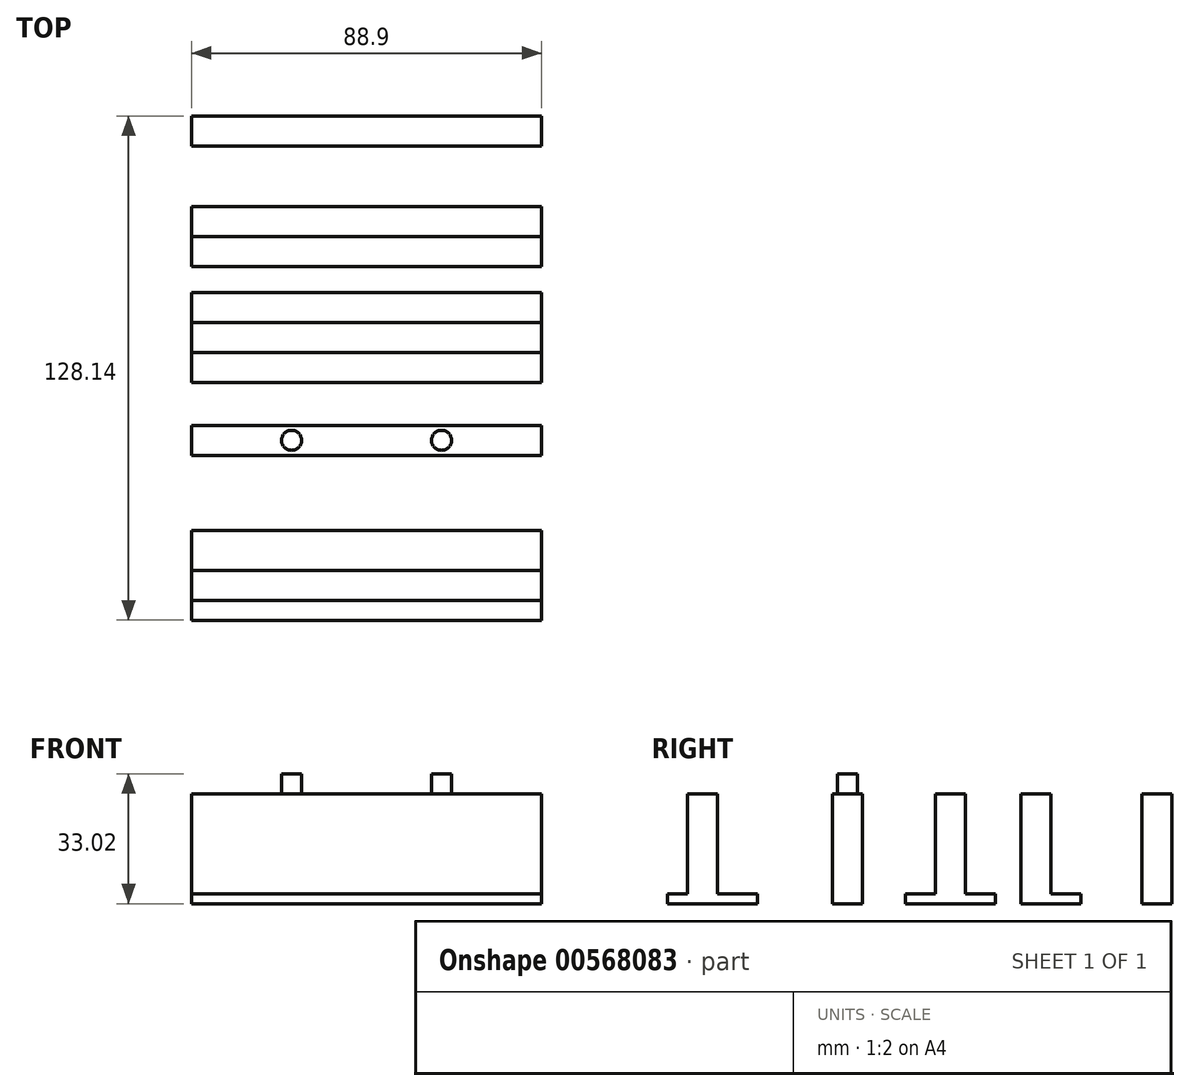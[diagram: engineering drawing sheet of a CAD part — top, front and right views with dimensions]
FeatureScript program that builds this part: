
annotation { "Feature Type Name" : "Feature", "Feature Type Description" : "" }
export const myFeature = defineFeature(function(context is Context, id is Id, definition is map)
    precondition{}
    {
        {
            var Q0;
            Q0=qCreatedBy(makeId("Top.planeOp"),FACE);
            var sketch = newSketch(context, id + "F0", { "sketchPlane" : qUnion([Q0])});
            skLineSegment(sketch, "E0.bottom", {"start": v(-25.4, 22.86) * mm, "end": v(63.5, 22.86) * mm});
            skLineSegment(sketch, "E0.top", {"start": v(-25.4, 15.24) * mm, "end": v(63.5, 15.24) * mm});
            skLineSegment(sketch, "E0.left", {"start": v(-25.4, 22.86) * mm, "end": v(-25.4, 15.24) * mm});
            skLineSegment(sketch, "E0.right", {"start": v(63.5, 22.86) * mm, "end": v(63.5, 15.24) * mm});
            skLineSegment(sketch, "E1.bottom", {"start": v(-25.4, 1.13) * mm, "end": v(63.5, 1.13) * mm});
            skLineSegment(sketch, "E1.top", {"start": v(-25.4, -6.5) * mm, "end": v(63.5, -6.5) * mm});
            skLineSegment(sketch, "E1.left", {"start": v(-25.4, 1.13) * mm, "end": v(-25.4, -6.5) * mm});
            skLineSegment(sketch, "E1.right", {"start": v(63.5, 1.13) * mm, "end": v(63.5, -6.5) * mm});
            skLineSegment(sketch, "E2.bottom", {"start": v(-25.4, -61.85) * mm, "end": v(63.5, -61.85) * mm});
            skLineSegment(sketch, "E2.top", {"start": v(-25.4, -69.47) * mm, "end": v(63.5, -69.47) * mm});
            skLineSegment(sketch, "E2.left", {"start": v(-25.4, -61.85) * mm, "end": v(-25.4, -69.47) * mm});
            skLineSegment(sketch, "E2.right", {"start": v(63.5, -61.85) * mm, "end": v(63.5, -69.47) * mm});
            skSolve(sketch);
        }
        {
            var Q0;
            Q0 = qSketchRegion(id + "F0", true);
            extrude(context, id + "F1", {"entities" : qUnion([Q0]), "depth" : 25.4 * mm, "offsetDistance" : 25.4 * mm});
        }
        {
            var Q0;
            Q0=qCreatedBy(makeId("Top.planeOp"),FACE);
            var sketch = newSketch(context, id + "F2", { "sketchPlane" : qUnion([Q0])});
            skLineSegment(sketch, "E3.bottom", {"start": v(-25.4, 30.48) * mm, "end": v(63.5, 30.48) * mm});
            skLineSegment(sketch, "E3.top", {"start": v(-25.4, 15.24) * mm, "end": v(63.5, 15.24) * mm});
            skLineSegment(sketch, "E3.left", {"start": v(-25.4, 30.48) * mm, "end": v(-25.4, 15.24) * mm});
            skLineSegment(sketch, "E3.right", {"start": v(63.5, 30.48) * mm, "end": v(63.5, 15.24) * mm});
            skLineSegment(sketch, "E4.bottom", {"start": v(-25.4, 8.75) * mm, "end": v(63.5, 8.75) * mm});
            skLineSegment(sketch, "E4.top", {"start": v(-25.4, -14.11) * mm, "end": v(63.5, -14.11) * mm});
            skLineSegment(sketch, "E4.left", {"start": v(-25.4, 8.75) * mm, "end": v(-25.4, -14.11) * mm});
            skLineSegment(sketch, "E4.right", {"start": v(63.5, 8.75) * mm, "end": v(63.5, -14.11) * mm});
            skLineSegment(sketch, "E5.bottom", {"start": v(-25.4, -51.7) * mm, "end": v(63.5, -51.7) * mm});
            skLineSegment(sketch, "E5.top", {"start": v(-25.4, -74.55) * mm, "end": v(63.5, -74.55) * mm});
            skLineSegment(sketch, "E5.left", {"start": v(-25.4, -51.7) * mm, "end": v(-25.4, -74.55) * mm});
            skLineSegment(sketch, "E5.right", {"start": v(63.5, -51.7) * mm, "end": v(63.5, -74.55) * mm});
            skSolve(sketch);
        }
        {
            var Q0;
            Q0 = qSketchRegion(id + "F2", true);
            extrude(context, id + "F3", {"entities" : qUnion([Q0]), "operationType" : NewBodyOperationType.ADD, "oppositeDirection" : true, "depth" : 2.54 * mm, "offsetDistance" : 25.4 * mm});
        }
        {
            var Q0;
            Q0=qCreatedBy(makeId("Top.planeOp"),FACE);
            cPlane(context, id + "F4", {"entities" : qUnion([Q0]), "cplaneType" : CPlaneType.OFFSET, "offset" : 2.54 * mm, "oppositeDirection" : true, "width" : 152.4 * mm, "height" : 152.4 * mm});
        }
        {
            var Q0;
            Q0=qCreatedBy(id+"F4.planeOp",FACE);
            var sketch = newSketch(context, id + "F5", { "sketchPlane" : qUnion([Q0])});
            skLineSegment(sketch, "E6.bottom", {"start": v(-25.4, -25.04) * mm, "end": v(63.5, -25.04) * mm});
            skLineSegment(sketch, "E6.top", {"start": v(-25.4, -32.66) * mm, "end": v(63.5, -32.66) * mm});
            skLineSegment(sketch, "E6.left", {"start": v(-25.4, -25.04) * mm, "end": v(-25.4, -32.66) * mm});
            skLineSegment(sketch, "E6.right", {"start": v(63.5, -25.04) * mm, "end": v(63.5, -32.66) * mm});
            skLineSegment(sketch, "E7.bottom", {"start": v(-25.4, 53.59) * mm, "end": v(63.5, 53.59) * mm});
            skLineSegment(sketch, "E7.top", {"start": v(-25.4, 45.97) * mm, "end": v(63.5, 45.97) * mm});
            skLineSegment(sketch, "E7.left", {"start": v(-25.4, 53.59) * mm, "end": v(-25.4, 45.97) * mm});
            skLineSegment(sketch, "E7.right", {"start": v(63.5, 53.59) * mm, "end": v(63.5, 45.97) * mm});
            skSolve(sketch);
        }
        {
            var Q0;
            Q0 = qSketchRegion(id + "F5", true);
            extrude(context, id + "F6", {"entities" : qUnion([Q0]), "depth" : 27.94 * mm, "offsetDistance" : 25.4 * mm});
        }
        {
            var Q0;
            Q0=qCreatedBy(makeId("Top.planeOp"),FACE);
            var sketch = newSketch(context, id + "F7", { "sketchPlane" : qUnion([Q0])});
            skCircle(sketch, "E8", {"center": v(38.1, -28.85) * mm, "radius": 2.54 * mm});
            skCircle(sketch, "E9", {"center": v(0, -28.85) * mm, "radius": 2.54 * mm});
            skSolve(sketch);
        }
        {
            var Q0;
            Q0 = qSketchRegion(id + "F7", true);
            extrude(context, id + "F8", {"entities" : qUnion([Q0]), "operationType" : NewBodyOperationType.ADD, "depth" : 30.48 * mm, "offsetDistance" : 25.4 * mm});
        }
    });
